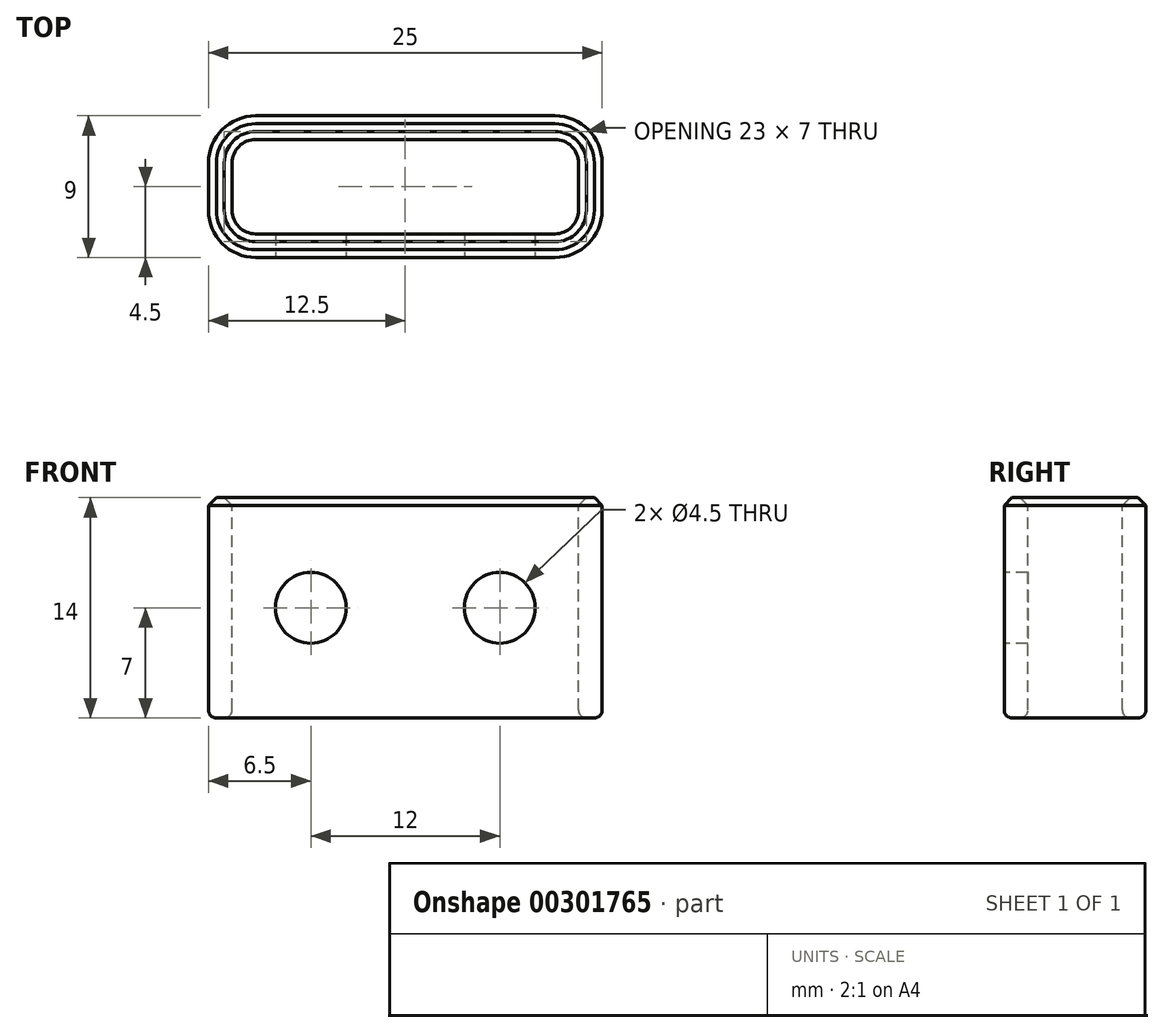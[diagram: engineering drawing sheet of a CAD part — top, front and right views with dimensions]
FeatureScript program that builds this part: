
annotation { "Feature Type Name" : "Feature", "Feature Type Description" : "" }
export const myFeature = defineFeature(function(context is Context, id is Id, definition is map)
    precondition{}
    {
        {
            var Q0;
            Q0=qCreatedBy(makeId("Top.planeOp"),FACE);
            var sketch = newSketch(context, id + "F0", { "sketchPlane" : qUnion([Q0])});
            skLineSegment(sketch, "E0.bottom", {"start": v(-9.5, -4.5) * mm, "end": v(9.5, -4.5) * mm});
            skLineSegment(sketch, "E0.top", {"start": v(-9.5, 4.5) * mm, "end": v(9.5, 4.5) * mm});
            skLineSegment(sketch, "E0.left", {"start": v(-12.5, -1.5) * mm, "end": v(-12.5, 1.5) * mm});
            skLineSegment(sketch, "E0.right", {"start": v(12.5, -1.5) * mm, "end": v(12.5, 1.5) * mm});
            skPoint(sketch, "E0.middle", {"position": v(0, 0) * mm});
            skPoint(sketch, "E1.visualSharp", {"position": v(-12.5, 4.5) * mm});
            skArc(sketch, "E1.filletArc", {"start": v(-9.5, 4.5) * mm, "mid": v(-11.62, 3.62) * mm, "end": v(-12.5, 1.5) * mm});
            skPoint(sketch, "E2.visualSharp", {"position": v(12.5, 4.5) * mm});
            skArc(sketch, "E2.filletArc", {"start": v(12.5, 1.5) * mm, "mid": v(11.62, 3.62) * mm, "end": v(9.5, 4.5) * mm});
            skPoint(sketch, "E3.visualSharp", {"position": v(12.5, -4.5) * mm});
            skArc(sketch, "E3.filletArc", {"start": v(9.5, -4.5) * mm, "mid": v(11.62, -3.62) * mm, "end": v(12.5, -1.5) * mm});
            skPoint(sketch, "E4.visualSharp", {"position": v(-12.5, -4.5) * mm});
            skArc(sketch, "E4.filletArc", {"start": v(-12.5, -1.5) * mm, "mid": v(-11.62, -3.62) * mm, "end": v(-9.5, -4.5) * mm});
            skSolve(sketch);
        }
        {
            var Q0;
            Q0 = qSketchRegion(id + "F0", true);
            extrude(context, id + "F1", {"entities" : qUnion([Q0]), "depth" : 14 * mm});
        }
        {
            var Q0;
            Q0=makeQuery(id+"F1.opExtrude","CAP_FACE",FACE,{"disambiguationData":[OSD([sQuery(id+"F0.wireOp",EDGE,"E0.bottom"),sQuery(id+"F0.wireOp",EDGE,"E0.top"),sQuery(id+"F0.wireOp",EDGE,"E0.left"),sQuery(id+"F0.wireOp",EDGE,"E0.right"),sQuery(id+"F0.wireOp",EDGE,"E1.filletArc"),sQuery(id+"F0.wireOp",EDGE,"E2.filletArc"),sQuery(id+"F0.wireOp",EDGE,"E3.filletArc"),sQuery(id+"F0.wireOp",EDGE,"E4.filletArc")])],"isStart":false});
            var Q1;
            Q1=makeQuery(id+"F1.opExtrude","CAP_FACE",FACE,{"disambiguationData":[OSD([sQuery(id+"F0.wireOp",EDGE,"E0.bottom"),sQuery(id+"F0.wireOp",EDGE,"E0.top"),sQuery(id+"F0.wireOp",EDGE,"E0.left"),sQuery(id+"F0.wireOp",EDGE,"E0.right"),sQuery(id+"F0.wireOp",EDGE,"E1.filletArc"),sQuery(id+"F0.wireOp",EDGE,"E2.filletArc"),sQuery(id+"F0.wireOp",EDGE,"E3.filletArc"),sQuery(id+"F0.wireOp",EDGE,"E4.filletArc")])],"isStart":true});
            shell(context, id + "F2", {"entities" : qUnion([Q0, Q1]), "thickness" : 1.5 * mm});
        }
        {
            var Q0;
            Q0=makeQuery(id+"F1.opExtrude","SWEPT_FACE",FACE,{"disambiguationData":[OSD([sQuery(id+"F0.wireOp",EDGE,"E0.bottom")])]});
            var sketch = newSketch(context, id + "F3", { "sketchPlane" : qUnion([Q0])});
            skCircle(sketch, "E5", {"center": v(-6, 7) * mm, "radius": 2.25 * mm});
            skCircle(sketch, "E6", {"center": v(6, 7) * mm, "radius": 2.25 * mm});
            skSolve(sketch);
        }
        {
            var Q0;
            Q0 = qSketchRegion(id + "F3", true);
            extrude(context, id + "F4", {"entities" : qUnion([Q0]), "operationType" : NewBodyOperationType.REMOVE, "oppositeDirection" : true, "depth" : 5 * mm});
        }
        {
            var Q0;
            Q0=makeQuery(id+"F1.opExtrude","CAP_EDGE",EDGE,{"disambiguationData":[OSD([sQuery(id+"F0.wireOp",EDGE,"E0.top")])],"isStart":true});
            var Q1;
            {var subQ0=sQuery(id+"F0.wireOp",EDGE,"E0.bottom");Q1=makeQuery(id+"F2.opShell","OFFSET_EDGE",EDGE,{"disambiguationData":[OSD([subQ0]),TDD([makeQuery(id+"F1.opExtrude","CAP_EDGE",EDGE,{"disambiguationData":[OSD([subQ0])],"isStart":true})])]});}
            var Q2;
            Q2=makeQuery(id+"F4.boolean.opBoolean","COPY",EDGE,{"derivedFrom":makeQuery(id+"F4.opExtrude","CAP_EDGE",EDGE,{"disambiguationData":[OSD([sQuery(id+"F3.wireOp",EDGE,"E6")])],"isStart":true})});
            var Q3;
            Q3=makeQuery(id+"F4.boolean.opBoolean","COPY",EDGE,{"derivedFrom":makeQuery(id+"F4.opExtrude","CAP_EDGE",EDGE,{"disambiguationData":[OSD([sQuery(id+"F3.wireOp",EDGE,"E5")])],"isStart":true})});
            fillet(context, id + "F5", {"entities" : qUnion([Q0, Q1, Q2, Q3]), "radius" : 0.5 * mm, "tangentPropagation" : true, "allowEdgeOverflow" : false});
        }
        {
            var Q0;
            Q0=makeQuery(id+"F1.opExtrude","CAP_EDGE",EDGE,{"disambiguationData":[OSD([sQuery(id+"F0.wireOp",EDGE,"E0.bottom")])],"isStart":false});
            var Q1;
            {var subQ0=sQuery(id+"F0.wireOp",EDGE,"E0.bottom");Q1=makeQuery(id+"F2.opShell","OFFSET_EDGE",EDGE,{"disambiguationData":[OSD([subQ0]),TDD([makeQuery(id+"F1.opExtrude","CAP_EDGE",EDGE,{"disambiguationData":[OSD([subQ0])],"isStart":false})])]});}
            chamfer(context, id + "F6", {"entities" : qUnion([Q0, Q1]), "width" : 0.5 * mm, "tangentPropagation" : true});
        }
    });
